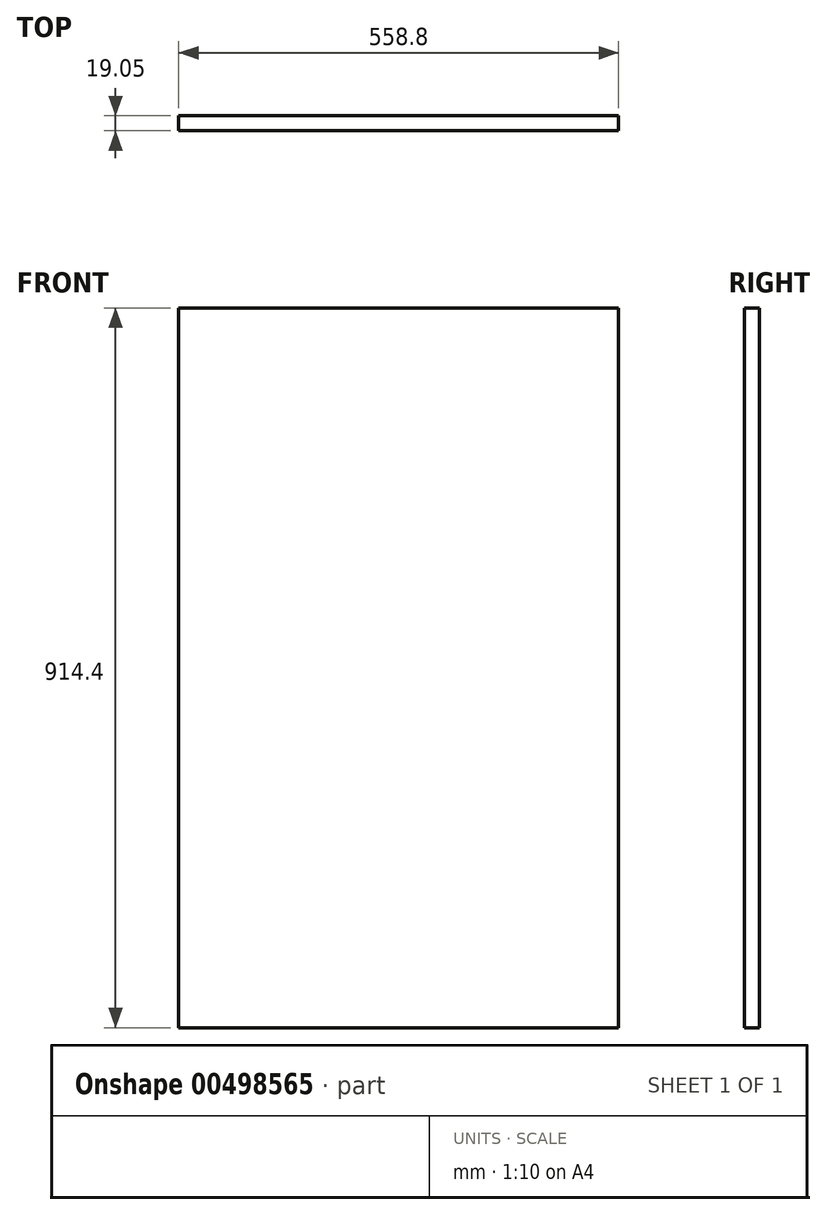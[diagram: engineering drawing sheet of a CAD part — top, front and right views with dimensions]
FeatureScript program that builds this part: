
annotation { "Feature Type Name" : "Feature", "Feature Type Description" : "" }
export const myFeature = defineFeature(function(context is Context, id is Id, definition is map)
    precondition{}
    {
        {
            var Q0;
            Q0=qCreatedBy(makeId("Front.planeOp"),FACE);
            var sketch = newSketch(context, id + "F0", { "sketchPlane" : qUnion([Q0])});
            skLineSegment(sketch, "E0.bottom", {"start": v(0, 0) * mm, "end": v(558.8, 0) * mm});
            skLineSegment(sketch, "E0.top", {"start": v(0, 914.4) * mm, "end": v(558.8, 914.4) * mm});
            skLineSegment(sketch, "E0.left", {"start": v(0, 0) * mm, "end": v(0, 914.4) * mm});
            skLineSegment(sketch, "E0.right", {"start": v(558.8, 0) * mm, "end": v(558.8, 914.4) * mm});
            skSolve(sketch);
        }
        {
            var Q0;
            Q0 = qSketchRegion(id + "F0", true);
            extrude(context, id + "F1", {"entities" : qUnion([Q0]), "depth" : 19.05 * mm, "offsetDistance" : 25.4 * mm});
        }
    });
